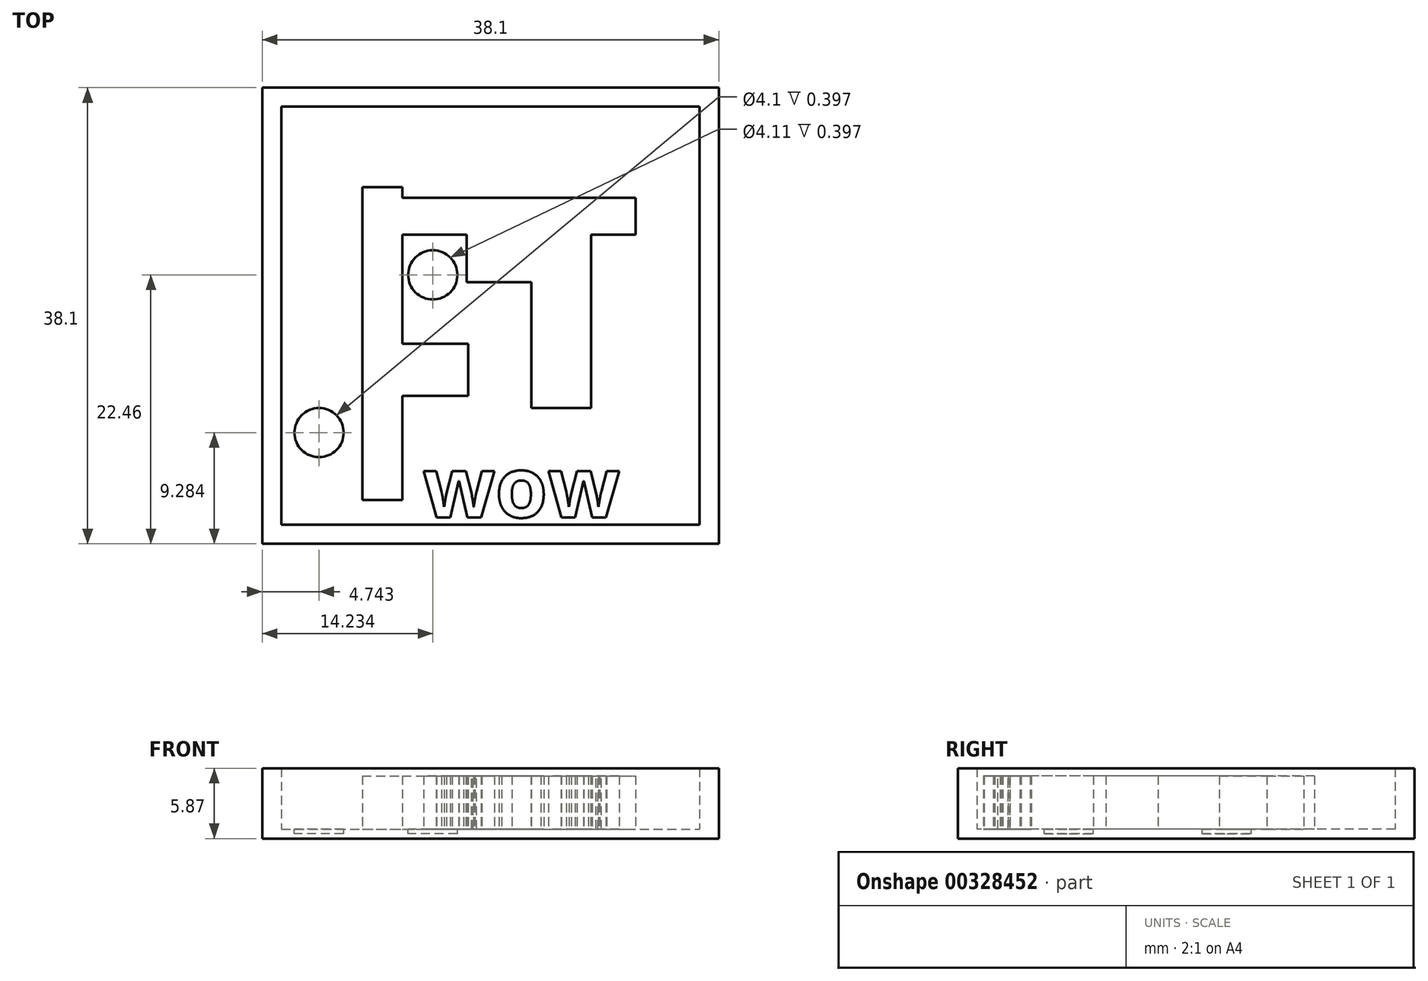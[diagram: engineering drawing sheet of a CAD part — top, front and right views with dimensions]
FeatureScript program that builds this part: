
annotation { "Feature Type Name" : "Feature", "Feature Type Description" : "" }
export const myFeature = defineFeature(function(context is Context, id is Id, definition is map)
    precondition{}
    {
        {
            var Q0;
            Q0=qCreatedBy(makeId("Top.planeOp"),FACE);
            var sketch = newSketch(context, id + "F0", { "sketchPlane" : qUnion([Q0])});
            skLineSegment(sketch, "E0.bottom", {"start": v(-19.62, 9.26) * mm, "end": v(18.48, 9.26) * mm});
            skLineSegment(sketch, "E0.top", {"start": v(-19.62, -28.84) * mm, "end": v(18.48, -28.84) * mm});
            skLineSegment(sketch, "E0.left", {"start": v(-19.62, 9.26) * mm, "end": v(-19.62, -28.84) * mm});
            skLineSegment(sketch, "E0.right", {"start": v(18.48, 9.26) * mm, "end": v(18.48, -28.84) * mm});
            skSolve(sketch);
        }
        {
            var Q0;
            Q0=makeQuery(id+"F0.imprint","IMPRINT",FACE,{"disambiguationData":[TD([[makeQuery(id+"F0.imprint","IMPRINT",EDGE,{"derivedFrom":sQuery(id+"F0.wireOp",EDGE,"E0.bottom")}),-1.0]])]});
            extrude(context, id + "F1", {"entities" : qUnion([Q0]), "depth" : 0.8 * mm});
        }
        {
            var Q0;
            Q0=makeQuery(id+"F1.opExtrude","CAP_FACE",FACE,{"disambiguationData":[OSD([sQuery(id+"F0.wireOp",EDGE,"E0.bottom"),sQuery(id+"F0.wireOp",EDGE,"E0.top"),sQuery(id+"F0.wireOp",EDGE,"E0.left"),sQuery(id+"F0.wireOp",EDGE,"E0.right")])],"isStart":false});
            var sketch = newSketch(context, id + "F2", { "sketchPlane" : qUnion([Q0])});
            skLineSegment(sketch, "E1.0", {"start": v(-18.02, 7.66) * mm, "end": v(16.88, 7.66) * mm});
            skLineSegment(sketch, "E1.1", {"start": v(-18.02, 7.66) * mm, "end": v(-18.02, -27.24) * mm});
            skLineSegment(sketch, "E1.2", {"start": v(-18.02, -27.24) * mm, "end": v(16.88, -27.24) * mm});
            skLineSegment(sketch, "E1.3", {"start": v(16.88, 7.66) * mm, "end": v(16.88, -27.24) * mm});
            skLineSegment(sketch, "E2.0", {"start": v(-25.97, 15.61) * mm, "end": v(-25.97, -35.19) * mm});
            skLineSegment(sketch, "E2.1", {"start": v(24.83, 15.61) * mm, "end": v(-25.97, 15.61) * mm});
            skLineSegment(sketch, "E2.2", {"start": v(24.83, -35.19) * mm, "end": v(24.83, 15.61) * mm});
            skLineSegment(sketch, "E2.3", {"start": v(-25.97, -35.19) * mm, "end": v(24.83, -35.19) * mm});
            skSolve(sketch);
        }
        {
            var Q0;
            Q0=makeQuery(id+"F2.imprint","IMPRINT",FACE,{"disambiguationData":[TD([[makeQuery(id+"F2.imprint","IMPRINT",EDGE,{"derivedFrom":sQuery(id+"F2.wireOp",EDGE,"E1.0")}),1.0]])]});
            extrude(context, id + "F3", {"entities" : qUnion([Q0]), "operationType" : NewBodyOperationType.ADD, "depth" : 5.08 * mm});
        }
        {
            var Q0;
            Q0=makeQuery(id+"F1.opExtrude","CAP_FACE",FACE,{"disambiguationData":[OSD([sQuery(id+"F0.wireOp",EDGE,"E0.bottom"),sQuery(id+"F0.wireOp",EDGE,"E0.top"),sQuery(id+"F0.wireOp",EDGE,"E0.left"),sQuery(id+"F0.wireOp",EDGE,"E0.right")])],"isStart":false});
            var sketch = newSketch(context, id + "F4", { "sketchPlane" : qUnion([Q0])});
            skLineSegment(sketch, "E3.bottom", {"start": v(-11.27, 0.94) * mm, "end": v(-7.94, 0.94) * mm});
            skLineSegment(sketch, "E3.top", {"start": v(-11.27, -25.2) * mm, "end": v(-7.94, -25.2) * mm});
            skLineSegment(sketch, "E3.left", {"start": v(-11.27, 0.94) * mm, "end": v(-11.27, -25.2) * mm});
            skLineSegment(sketch, "E3.right", {"start": v(-7.94, 0.94) * mm, "end": v(-7.94, 0.05) * mm});
            skLineSegment(sketch, "E4.bottom", {"start": v(-7.94, -3.03) * mm, "end": v(-2.55, -3.03) * mm});
            skLineSegment(sketch, "E4.top", {"start": v(-7.94, 0.05) * mm, "end": v(11.54, 0.05) * mm});
            skLineSegment(sketch, "E4.right", {"start": v(11.54, -3.03) * mm, "end": v(11.54, 0.05) * mm});
            skLineSegment(sketch, "E5.top", {"start": v(2.83, -17.5) * mm, "end": v(7.82, -17.5) * mm});
            skLineSegment(sketch, "E5.left", {"start": v(2.83, -7) * mm, "end": v(2.83, -17.5) * mm});
            skLineSegment(sketch, "E5.right", {"start": v(7.82, -3.03) * mm, "end": v(7.82, -17.5) * mm});
            skLineSegment(sketch, "E6.bottom", {"start": v(-7.94, -12.12) * mm, "end": v(-2.43, -12.12) * mm});
            skLineSegment(sketch, "E6.top", {"start": v(-7.94, -16.48) * mm, "end": v(-2.43, -16.48) * mm});
            skLineSegment(sketch, "E6.right", {"start": v(-2.43, -12.12) * mm, "end": v(-2.43, -16.48) * mm});
            skLineSegment(sketch, "E7.top", {"start": v(-7.94, -27.24) * mm, "end": v(16.88, -27.24) * mm});
            skLineSegment(sketch, "E7.right", {"start": v(16.88, -25.2) * mm, "end": v(16.88, -27.24) * mm});
            skLineSegment(sketch, "E8.bottom", {"start": v(2.83, -7) * mm, "end": v(-2.55, -7) * mm});
            skLineSegment(sketch, "E8.right", {"start": v(-2.55, -7) * mm, "end": v(-2.55, -3.03) * mm});
            skLineSegment(sketch, "E9.trimOffspring", {"start": v(-7.94, -16.48) * mm, "end": v(-7.94, -25.2) * mm});
            skLineSegment(sketch, "E10.trimOffspring", {"start": v(7.82, -3.03) * mm, "end": v(11.54, -3.03) * mm});
            skLineSegment(sketch, "E11.trimOffspring", {"start": v(-7.94, -3.03) * mm, "end": v(-7.94, -12.12) * mm});
            skCircle(sketch, "E12", {"center": v(-14.88, -19.56) * mm, "radius": 2.05 * mm});
            skCircle(sketch, "E13", {"center": v(-5.39, -6.38) * mm, "radius": 2.05 * mm});
            skSolve(sketch);
        }
        {
            var Q0;
            Q0=makeQuery(id+"F4.imprint","IMPRINT",FACE,{"disambiguationData":[TD([[makeQuery(id+"F4.imprint","IMPRINT",EDGE,{"derivedFrom":sQuery(id+"F4.wireOp",EDGE,"E3.bottom")}),-1.0]])]});
            extrude(context, id + "F5", {"entities" : qUnion([Q0]), "operationType" : NewBodyOperationType.ADD, "depth" : 4.44 * mm});
        }
        {
            var Q0;
            Q0=makeQuery(id+"F4.imprint","IMPRINT",FACE,{"disambiguationData":[TD([[makeQuery(id+"F4.imprint","IMPRINT",EDGE,{"derivedFrom":sQuery(id+"F4.wireOp",EDGE,"E13")}),1.0]])]});
            var Q1;
            {var subQ0=sQuery(id+"F4.wireOp",EDGE,"E12");var subQ1=makeQuery(id+"F3.opExtrude","CAP_EDGE",EDGE,{"disambiguationData":[OSD([sQuery(id+"F2.wireOp",EDGE,"E1.1")])],"isStart":true});var subQ2=makeQuery(id+"F4.imprint","INTERSECT",VERTEX,{"disambiguationData":[OD(0.0)],"derivedFrom":[subQ1,subQ0]});Q1=makeQuery(id+"F4.imprint","IMPRINT",FACE,{"disambiguationData":[TD([[makeQuery(id+"F4.imprint","IMPRINT",EDGE,{"disambiguationData":[TD([[subQ2,1.0]])],"derivedFrom":subQ0}),1.0]])]});}
            extrude(context, id + "F6", {"entities" : qUnion([Q0, Q1]), "operationType" : NewBodyOperationType.REMOVE, "oppositeDirection" : true, "depth" : 0.4 * mm});
        }
        {
            var Q0;
            Q0=makeQuery(id+"F4.imprint","IMPRINT",FACE,{"disambiguationData":[TD([[makeQuery(id+"F4.imprint","IMPRINT",EDGE,{"derivedFrom":sQuery(id+"F4.wireOp",EDGE,"E3.bottom")}),1.0]])]});
            var sketch = newSketch(context, id + "F7", { "sketchPlane" : qUnion([Q0])});
            skText(sketch, "E14", { "text": "wow", "fontName": "OpenSans-Bold.ttf"});
            const initialGuessF7  = {"E14": [-0.00622, -0.02663, 1, 0, 0.00508]};
            skSetInitialGuess(sketch, initialGuessF7);
            skSolve(sketch);
        }
        {
            var Q0;
            Q0 = qSketchRegion(id + "F7", true);
            extrude(context, id + "F8", {"entities" : qUnion([Q0]), "operationType" : NewBodyOperationType.ADD, "depth" : 4.44 * mm});
        }
    });
